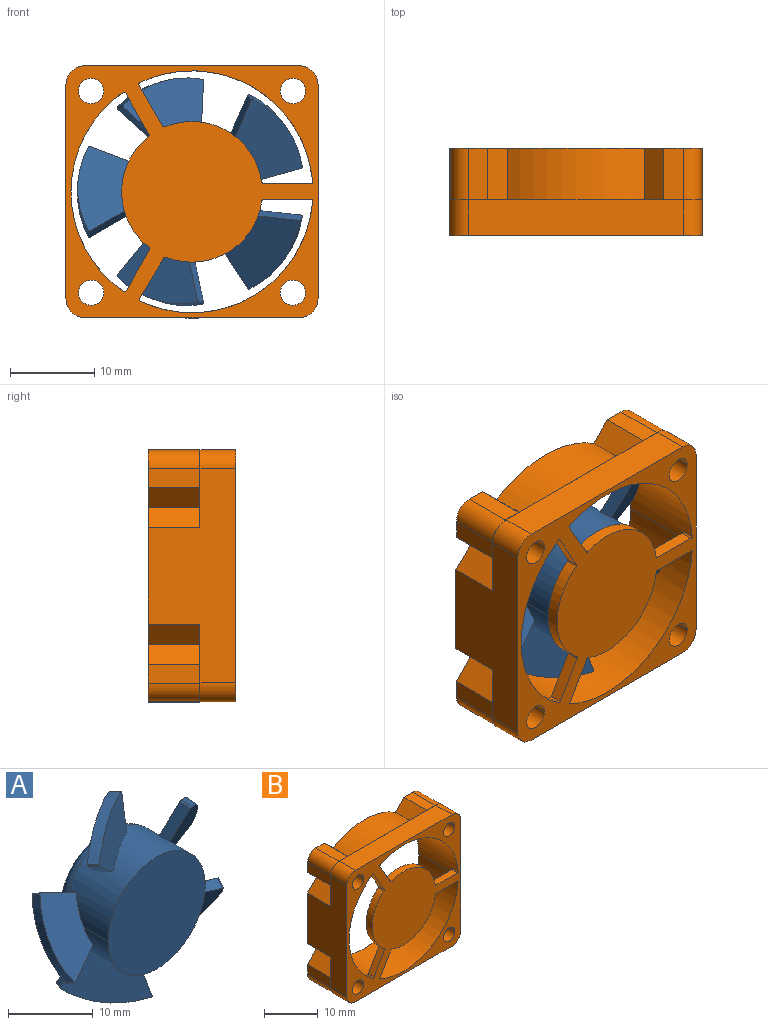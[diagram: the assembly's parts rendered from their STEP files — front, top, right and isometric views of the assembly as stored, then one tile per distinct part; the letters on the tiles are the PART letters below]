
ASSEMBLY  parts=2 mates=1
PART A: 42 faces, bbox 26.8x9x27.2 mm
  f0: plane 16.24x16.24mm, normal (0,-1,0), area 207.2mm2, adj f38,f39
  f1: cylinder r=13.61mm len=8.58mm, axis (-0.29,-0.87,-0.4), area 17.6mm2, adj f2,f4,f5,f6
  f2: cylinder r=0.19mm len=1.35mm, axis (-0.29,-0.87,-0.4), area 0.5mm2, adj f1,f3,f4,f6
  f3: plane 5.33x2.79mm, normal (-0.02,-0.42,0.91), area 7.8mm2, adj f2,f4,f6,f38
  f4: plane 8.93x8.79mm, normal (-0.29,-0.87,-0.4), area 51.4mm2, adj f1,f2,f3,f5,f7,f38
  f5: cylinder r=0.19mm len=1.35mm, axis (-0.29,-0.87,-0.4), area 0.4mm2, adj f1,f4,f6,f7
  f6: plane 8.78x8.72mm, normal (0.29,0.87,0.4), area 51.1mm2, adj f1,f2,f3,f5,f7,f37,f38
  f7: plane 4.67x3.26mm, normal (-0.79,0.46,-0.41), area 7.6mm2, adj f4,f5,f6,f37,f38
  f8: cylinder r=13.61mm len=10.09mm, axis (-0.48,-0.87,0.15), area 17.6mm2, adj f9,f11,f12,f13
  f9: cylinder r=0.19mm len=1.35mm, axis (-0.48,-0.87,0.15), area 0.5mm2, adj f8,f10,f11,f13
  f10: plane 5.04x2.79mm, normal (0.86,-0.42,0.3), area 7.8mm2, adj f9,f11,f13,f38
  f11: plane 9.64x7.55mm, normal (-0.48,-0.87,0.15), area 51.4mm2, adj f8,f9,f10,f12,f14,f38
  f12: cylinder r=0.19mm len=1.35mm, axis (-0.48,-0.87,0.15), area 0.4mm2, adj f8,f11,f13,f14
  f13: plane 9.6x7.28mm, normal (0.48,0.87,-0.15), area 51.1mm2, adj f8,f9,f10,f12,f14,f37,f38
  f14: plane 4.25x3.75mm, normal (-0.63,0.46,0.63), area 7.6mm2, adj f11,f12,f13,f37,f38
  f15: cylinder r=13.61mm len=10.61mm, axis (0,-0.87,0.5), area 17.6mm2, adj f16,f18,f19,f21
  f16: cylinder r=0.19mm len=1.35mm, axis (0,-0.87,0.5), area 0.5mm2, adj f15,f17,f18,f21
  f17: plane 4.47x3.21mm, normal (0.55,-0.42,-0.72), area 7.8mm2, adj f16,f18,f21,f38
  f18: plane 10.1x6.36mm, normal (0,-0.87,0.5), area 51.4mm2, adj f15,f16,f17,f19,f22,f38,f39
  f19: cylinder r=0.19mm len=1.35mm, axis (0,-0.87,0.5), area 0.4mm2, adj f15,f18,f21,f22
  f20: cylinder r=8.12mm len=2.74mm, axis (0,1,0), area 2.2mm2, adj f21,f36,f38
  f21: plane 10.07x6.05mm, normal (0,0.87,-0.5), area 51.1mm2, adj f15,f16,f17,f19,f20,f22,f36,f38
  f22: plane 4.81x2.47mm, normal (0.4,0.46,0.79), area 7.6mm2, adj f18,f19,f21,f36,f39
  f23: cylinder r=13.61mm len=10.09mm, axis (0.48,-0.87,0.15), area 17.6mm2, adj f24,f26,f27,f28
  f24: cylinder r=0.19mm len=1.35mm, axis (0.48,-0.87,0.15), area 0.5mm2, adj f23,f25,f26,f28
  f25: plane 4.37x3.69mm, normal (-0.51,-0.42,-0.75), area 7.8mm2, adj f24,f26,f28,f39
  f26: plane 9.64x6.85mm, normal (0.48,-0.87,0.15), area 51.4mm2, adj f23,f24,f25,f27,f29,f39
  f27: cylinder r=0.19mm len=1.35mm, axis (0.48,-0.87,0.15), area 0.4mm2, adj f23,f26,f28,f29
  f28: plane 9.6x6.97mm, normal (-0.48,0.87,-0.15), area 51.1mm2, adj f23,f24,f25,f27,f29,f36,f39
  f29: plane 5.14x2.36mm, normal (0.88,0.46,-0.14), area 7.6mm2, adj f26,f27,f28,f36,f39
  f30: cylinder r=0.19mm len=1.35mm, axis (0.29,-0.87,-0.4), area 0.4mm2, adj f33,f34,f40,f41
  f31: cylinder r=0.19mm len=1.35mm, axis (0.29,-0.87,-0.4), area 0.5mm2, adj f32,f33,f40,f41
  f32: plane 5.1x2.79mm, normal (-0.87,-0.42,0.26), area 7.8mm2, adj f31,f33,f39,f40
  f33: plane 9.62x8.13mm, normal (0.29,-0.87,-0.4), area 51.4mm2, adj f30,f31,f32,f34,f39,f41
  f34: plane 5.12x2.36mm, normal (0.14,0.46,-0.88), area 7.6mm2, adj f30,f33,f36,f39,f40
  f35: plane 13.24x13.24mm, normal (0,1,0), area 137.7mm2, adj f36,f37
  f36: torus R=6.62mm, axis (0,1,0), area 56mm2, adj f20,f21,f22,f28,f29,f34,f35,f37
  f37: torus R=6.62mm, axis (0,1,0), area 56.1mm2, adj f6,f7,f13,f14,f35,f36,f38
  f38: cylinder r=8.12mm len=16.24mm, axis (0,-1,0), area 163.9mm2, adj f0,f3,f4,f6,f7,f10,f11,f13
  f39: cylinder r=8.12mm len=16.24mm, axis (0,-1,0), area 160.3mm2, adj f0,f18,f22,f25,f26,f28,f29,f32
  f40: plane 9.5x8.18mm, normal (-0.29,0.87,0.4), area 51.1mm2, adj f30,f31,f32,f34,f36,f39,f41
  f41: cylinder r=13.61mm len=8.58mm, axis (0.29,-0.87,-0.4), area 17.6mm2, adj f30,f31,f33,f40
PART B: 84 faces, bbox 30x10.4x30 mm
  f0: plane 6.15x2.4mm, normal (0.7,0,0.72), area 20.6mm2, adj f9,f10,f13,f19
  f1: plane 6.15x2.33mm, normal (-0.72,0,0.7), area 20mm2, adj f7,f10,f11,f19
  f2: plane 6.15x2.4mm, normal (0.72,0,-0.7), area 20.6mm2, adj f7,f8,f12,f19
  f3: plane 6.15x2.33mm, normal (0.7,0,0.72), area 20mm2, adj f6,f8,f18,f19
  f4: plane 6.15x2.36mm, normal (-0.7,0,-0.72), area 20.2mm2, adj f6,f15,f17,f19
  f5: plane 6.15x2.32mm, normal (0.72,0,-0.7), area 19.9mm2, adj f14,f15,f16,f19
  f6: plane 15x13.79mm, normal (0,1,0), area 18.6mm2, adj f3,f4,f8,f15,f17,f18,f54,f57
  f7: plane 15x15mm, normal (0,1,0), area 19.1mm2, adj f1,f2,f8,f10,f11,f12,f21,f54
  f8: cylinder r=15.03mm len=16.33mm, axis (0,-1,0), area 106.1mm2, adj f2,f3,f6,f7,f19
  f9: plane 15x9.24mm, normal (0,1,0), area 15.6mm2, adj f0,f10,f13,f20,f55,f68,f69,f70
  f10: cylinder r=15.03mm len=16.33mm, axis (0,-1,0), area 106.1mm2, adj f0,f1,f7,f9,f19
  f11: plane 6.15x2.29mm, normal (0,0,1), area 14.1mm2, adj f1,f7,f19,f72
  f12: plane 6.15x2.24mm, normal (1,0,0), area 13.8mm2, adj f2,f7,f19,f72
  f13: plane 6.15x2.25mm, normal (0,0,1), area 13.8mm2, adj f0,f9,f19,f71
  f14: plane 13.88x9.24mm, normal (0,1,0), area 15.4mm2, adj f5,f15,f16,f55,f56,f57,f67,f74
  f15: cylinder r=15.03mm len=16.38mm, axis (0,-1,0), area 106.6mm2, adj f4,f5,f6,f14,f19,f77
  f16: plane 6.15x2.28mm, normal (0,0,-1), area 14.1mm2, adj f5,f14,f19,f74
  f17: plane 6.15x2.24mm, normal (0,0,-1), area 13.8mm2, adj f4,f6,f19,f73
  f18: plane 6.15x2.29mm, normal (1,0,0), area 14.1mm2, adj f3,f6,f19,f73
  f19: plane 30.05x30mm, normal (0,1,0), area 112mm2, adj f0,f1,f2,f3,f4,f5,f8,f10
  f20: cylinder r=2.26mm len=4.25mm, axis (0,-1,0), area 15.1mm2, adj f9,f22,f55,f83
  f21: cylinder r=2.26mm len=4.25mm, axis (0,-1,0), area 15.1mm2, adj f7,f22,f54,f83
  f22: plane 30x30mm, normal (0,-1,0), area 470.6mm2, adj f20,f21,f23,f24,f25,f26,f27,f28
  f23: cylinder r=1.5mm len=10.15mm, axis (0,1,0), area 47.8mm2, adj f22,f24,f81
  f24: cylinder r=1.5mm len=10.15mm, axis (0,1,0), area 47.8mm2, adj f22,f23,f81
  f25: cylinder r=1.5mm len=10.15mm, axis (0,1,0), area 47.8mm2, adj f22,f26,f82
  f26: cylinder r=1.5mm len=10.15mm, axis (0,1,0), area 47.8mm2, adj f22,f25,f82
  f27: cylinder r=1.5mm len=10.15mm, axis (0,1,0), area 47.8mm2, adj f22,f28,f79
  f28: cylinder r=1.5mm len=10.15mm, axis (0,1,0), area 47.8mm2, adj f22,f27,f79
  f29: cylinder r=1.5mm len=10.15mm, axis (0,1,0), area 47.8mm2, adj f22,f30,f80
  f30: cylinder r=1.5mm len=10.15mm, axis (0,1,0), area 47.8mm2, adj f22,f29,f80
  f31: plane 5.67x1.5mm, normal (0.01,0,1), area 8.5mm2, adj f22,f32,f38,f78
  f32: cylinder r=0.2mm len=1.5mm, axis (0,1,0), area 0.4mm2, adj f22,f31,f33,f78
  f33: cylinder r=8.37mm len=11.5mm, axis (0,-1,0), area 22.9mm2, adj f22,f32,f34,f78
  f34: cylinder r=0.2mm len=1.5mm, axis (0,1,0), area 0.4mm2, adj f22,f33,f35,f78
  f35: plane 4.9x2.83mm, normal (0.87,0,0.5), area 8.5mm2, adj f22,f34,f36,f78
  f36: cylinder r=0.2mm len=1.5mm, axis (0,1,0), area 0.5mm2, adj f22,f35,f37,f78
  f37: cylinder r=14.4mm len=28.8mm, axis (0,1,0), area 465.2mm2, adj f19,f22,f36,f38,f45,f47,f78
  f38: cylinder r=0.2mm len=1.5mm, axis (0,1,0), area 0.5mm2, adj f22,f31,f37,f78
  f39: plane 4.88x2.89mm, normal (0.86,0,-0.51), area 8.5mm2, adj f22,f40,f46,f78
  f40: cylinder r=0.2mm len=1.5mm, axis (0,1,0), area 0.4mm2, adj f22,f39,f41,f78
  f41: cylinder r=8.37mm len=11.41mm, axis (0,-1,0), area 22.9mm2, adj f22,f40,f42,f78
  f42: cylinder r=0.2mm len=1.5mm, axis (0,1,0), area 0.4mm2, adj f22,f41,f43,f78
  f43: plane 5.66x1.5mm, normal (0,0,-1), area 8.5mm2, adj f22,f42,f44,f78
  f44: cylinder r=0.2mm len=1.5mm, axis (0,1,0), area 0.5mm2, adj f22,f43,f45,f78
  f45: cylinder r=14.4mm len=28.8mm, axis (0,1,0), area 465.3mm2, adj f19,f22,f37,f44,f46,f53,f78
  f46: cylinder r=0.2mm len=1.5mm, axis (0,1,0), area 0.5mm2, adj f22,f39,f45,f78
  f47: cylinder r=0.2mm len=1.5mm, axis (0,1,0), area 0.5mm2, adj f22,f37,f48,f78
  f48: plane 4.94x2.78mm, normal (-0.87,0,-0.49), area 8.5mm2, adj f22,f47,f49,f78
  f49: cylinder r=0.2mm len=1.5mm, axis (0,1,0), area 0.4mm2, adj f22,f48,f50,f78
  f50: cylinder r=8.37mm len=13.23mm, axis (0,-1,0), area 22.9mm2, adj f22,f49,f51,f78
  f51: cylinder r=0.2mm len=1.5mm, axis (0,1,0), area 0.4mm2, adj f22,f50,f52,f78
  f52: plane 4.9x2.82mm, normal (-0.87,0,0.5), area 8.5mm2, adj f22,f51,f53,f78
  f53: cylinder r=0.2mm len=1.5mm, axis (0,1,0), area 0.5mm2, adj f22,f45,f52,f78
  f54: plane 25.48x4.25mm, normal (1,0,0), area 108.3mm2, adj f6,f7,f21,f22,f58
  f55: plane 25.48x10.4mm, normal (-1,0,0), area 179.1mm2, adj f9,f14,f19,f20,f22,f56,f67,f68
  f56: cylinder r=2.26mm len=4.25mm, axis (0,-1,0), area 15.1mm2, adj f14,f22,f55,f57
  f57: plane 25.48x4.25mm, normal (0,0,-1), area 108.3mm2, adj f6,f14,f22,f56,f58,f77
  f58: cylinder r=2.26mm len=4.25mm, axis (0,-1,0), area 15.1mm2, adj f6,f22,f54,f57
  f59: cylinder r=2.25mm len=4.5mm, axis (0,-1,0), area 1.8mm2, adj f19,f60,f79
  f60: cylinder r=2.25mm len=4.5mm, axis (0,-1,0), area 1.8mm2, adj f19,f59,f79
  f61: cylinder r=2.25mm len=4.5mm, axis (0,-1,0), area 1.8mm2, adj f19,f62,f80
  f62: cylinder r=2.25mm len=4.5mm, axis (0,-1,0), area 1.8mm2, adj f19,f61,f80
  f63: cylinder r=2.25mm len=4.5mm, axis (0,-1,0), area 1.8mm2, adj f19,f64,f81
  f64: cylinder r=2.25mm len=4.5mm, axis (0,-1,0), area 1.8mm2, adj f19,f63,f81
  f65: cylinder r=2.25mm len=4.5mm, axis (0,-1,0), area 1.8mm2, adj f19,f66,f82
  f66: cylinder r=2.25mm len=4.5mm, axis (0,-1,0), area 1.8mm2, adj f19,f65,f82
  f67: plane 6.15x2.39mm, normal (-0.7,0,-0.71), area 20.7mm2, adj f14,f19,f55,f76
  f68: plane 6.15x2.44mm, normal (-0.7,0,0.71), area 21.1mm2, adj f9,f19,f55,f69
  f69: plane 6.15x2.34mm, normal (-0.7,0,-0.72), area 20.1mm2, adj f9,f19,f68,f70
  f70: plane 6.15x2.28mm, normal (-1,0,0), area 14.1mm2, adj f9,f19,f69,f71
  f71: cylinder r=2.16mm len=6.15mm, axis (0,-1,0), area 20.9mm2, adj f9,f13,f19,f70
  f72: cylinder r=2.16mm len=6.15mm, axis (0,-1,0), area 20.9mm2, adj f7,f11,f12,f19
  f73: cylinder r=2.16mm len=6.15mm, axis (0,-1,0), area 20.9mm2, adj f6,f17,f18,f19
  f74: cylinder r=2.16mm len=6.15mm, axis (0,-1,0), area 20.9mm2, adj f14,f16,f19,f75
  f75: plane 6.15x2.25mm, normal (-1,0,0), area 13.8mm2, adj f14,f19,f74,f76
  f76: plane 6.15x2.4mm, normal (-0.72,0,0.7), area 20.6mm2, adj f14,f19,f67,f75
  f77: plane 2.32x0.05mm, normal (0,-1,0), area 0.1mm2, adj f15,f57
  f78: plane 26.01x22.77mm, normal (0,1,0), area 254.6mm2, adj f31,f32,f33,f34,f35,f36,f37,f38
  f79: plane 4.5x4.5mm, normal (0,1,0), area 8.8mm2, adj f27,f28,f59,f60
  f80: plane 4.5x4.5mm, normal (0,1,0), area 8.8mm2, adj f29,f30,f61,f62
  f81: plane 4.5x4.5mm, normal (0,1,0), area 8.8mm2, adj f23,f24,f63,f64
  f82: plane 4.5x4.5mm, normal (0,1,0), area 8.8mm2, adj f25,f26,f65,f66
  f83: plane 25.48x4.25mm, normal (0,0,1), area 108.3mm2, adj f7,f9,f20,f21,f22
PLACE A at identity
PLACE B at identity fixed
MATE revolute B.f45 <-> A.f38  axis (0,1,0) through (0,-8.9,0)mm
